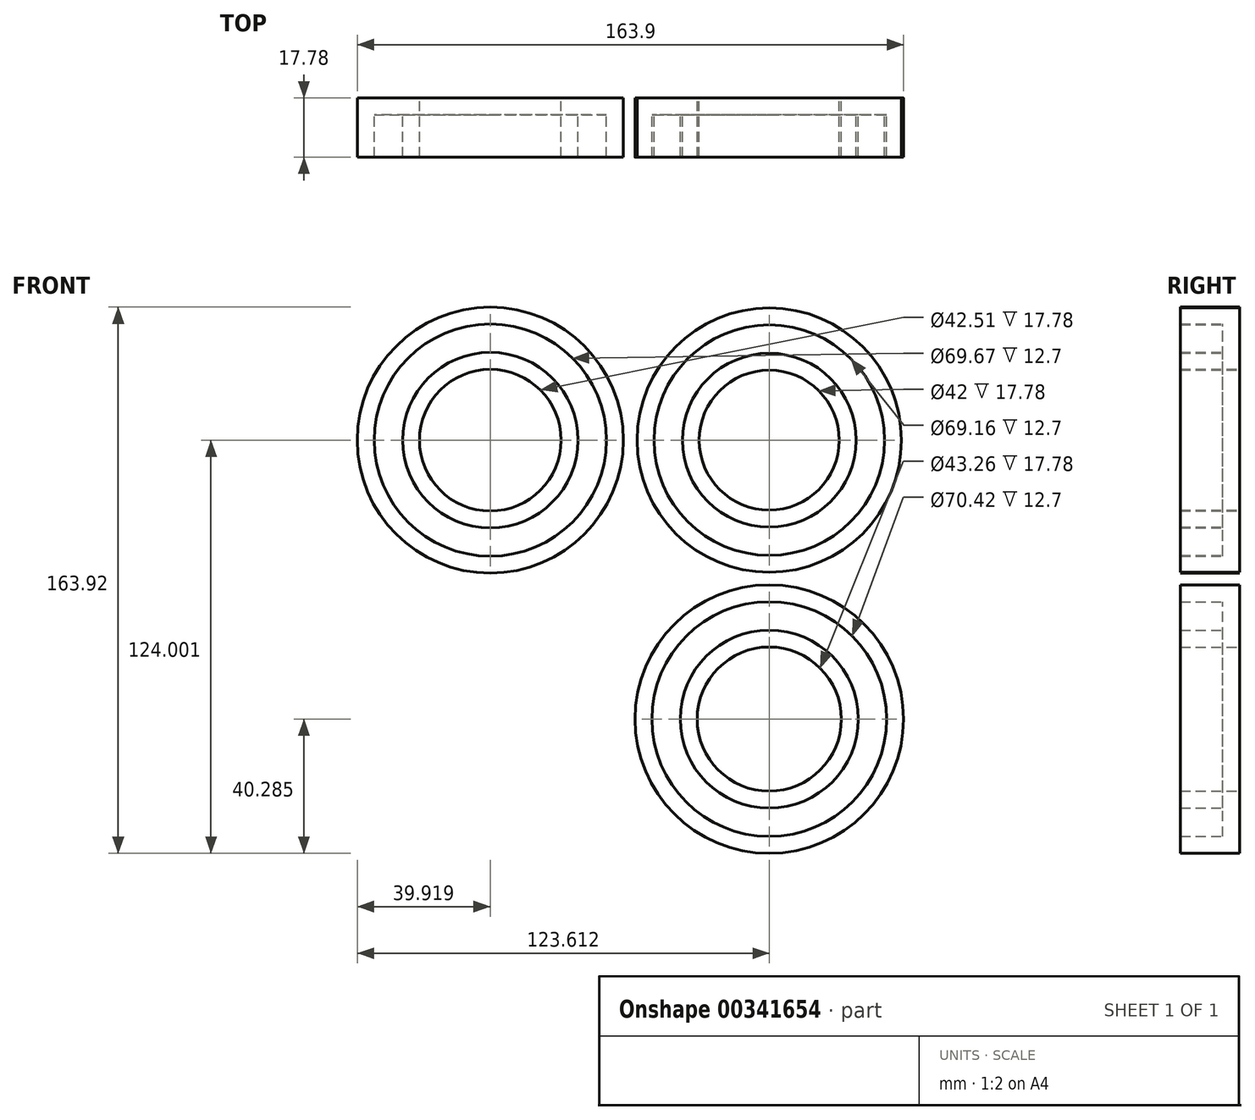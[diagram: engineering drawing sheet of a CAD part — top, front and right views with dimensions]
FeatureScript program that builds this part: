
annotation { "Feature Type Name" : "Feature", "Feature Type Description" : "" }
export const myFeature = defineFeature(function(context is Context, id is Id, definition is map)
    precondition{}
    {
        {
            var Q0;
            Q0=qCreatedBy(makeId("Front.planeOp"),FACE);
            var sketch = newSketch(context, id + "F0", { "sketchPlane" : qUnion([Q0])});
            skCircle(sketch, "E0", {"center": v(-41.16, 43.42) * mm, "radius": 34.83 * mm});
            skCircle(sketch, "E1", {"center": v(42.53, 43.42) * mm, "radius": 34.58 * mm});
            skCircle(sketch, "E2", {"center": v(42.53, -40.3) * mm, "radius": 35.2 * mm});
            skCircle(sketch, "E3", {"center": v(-41.16, 43.42) * mm, "radius": 26.33 * mm});
            skCircle(sketch, "E4", {"center": v(42.53, 43.42) * mm, "radius": 26.08 * mm});
            skCircle(sketch, "E5", {"center": v(42.53, -40.3) * mm, "radius": 26.7 * mm});
            skPoint(sketch, "E6.center.orphan", {"position": v(-41.16, -40.3) * mm});
            skSolve(sketch);
        }
        {
            var Q0;
            Q0=qSketchRegion(id+"F0",true);
            extrude(context, id + "F1", {"entities" : qUnion([Q0]), "depth" : 12.7 * mm});
        }
        {
            var Q0;
            Q0=qSketchRegion(id+"F0",true);
            extrude(context, id + "F2", {"entities" : qUnion([Q0]), "operationType" : NewBodyOperationType.ADD, "depth" : 12.7 * mm});
        }
        {
            var Q0;
            Q0=makeQuery(id+"F1.opExtrude","CAP_FACE",FACE,{"disambiguationData":[OSD([sQuery(id+"F0.wireOp",EDGE,"E0"),sQuery(id+"F0.wireOp",EDGE,"E1"),sQuery(id+"F0.wireOp",EDGE,"E2"),sQuery(id+"F0.wireOp",EDGE,"E6"),sQuery(id+"F0.wireOp",EDGE,"E3"),sQuery(id+"F0.wireOp",EDGE,"E4"),sQuery(id+"F0.wireOp",EDGE,"E5"),sQuery(id+"F0.wireOp",EDGE,"wCtjPolj-I49G-lrQl-AUey-eViT78JExmOk"),sQuery(id+"F0.wireOp",EDGE,"aY4H54qb-RbTj-2kDe-gUlC-NX0kmxSkIGok"),sQuery(id+"F0.wireOp",EDGE,"1Y8Dx6uG-hAqN-YXqH-EnJb-ngNhOZ5jz4mU"),sQuery(id+"F0.wireOp",EDGE,"CCXHPMnO-ZX1g-oIHU-5eSa-8MNjUUb0rYb2"),sQuery(id+"F0.wireOp",EDGE,"ZSUHFdVn-9fsU-8JFY-LW2a-uvZyDMq4o9Ci")])],"isStart":false});
            var Q1;
            Q1=makeQuery(id+"F1.opExtrude","SWEPT_BODY",BODY,{"disambiguationData":[OSD([sQuery(id+"F0.wireOp",EDGE,"E0"),sQuery(id+"F0.wireOp",EDGE,"E1"),sQuery(id+"F0.wireOp",EDGE,"E2"),sQuery(id+"F0.wireOp",EDGE,"E6"),sQuery(id+"F0.wireOp",EDGE,"E3"),sQuery(id+"F0.wireOp",EDGE,"E4"),sQuery(id+"F0.wireOp",EDGE,"E5"),sQuery(id+"F0.wireOp",EDGE,"wCtjPolj-I49G-lrQl-AUey-eViT78JExmOk"),sQuery(id+"F0.wireOp",EDGE,"aY4H54qb-RbTj-2kDe-gUlC-NX0kmxSkIGok"),sQuery(id+"F0.wireOp",EDGE,"1Y8Dx6uG-hAqN-YXqH-EnJb-ngNhOZ5jz4mU"),sQuery(id+"F0.wireOp",EDGE,"CCXHPMnO-ZX1g-oIHU-5eSa-8MNjUUb0rYb2"),sQuery(id+"F0.wireOp",EDGE,"ZSUHFdVn-9fsU-8JFY-LW2a-uvZyDMq4o9Ci")])]});
            shell(context, id + "F3", {"entities" : qUnion([Q0]), "parts" : qUnion([Q1]), "thickness" : 5.08 * mm, "oppositeDirection" : true});
        }
    });
